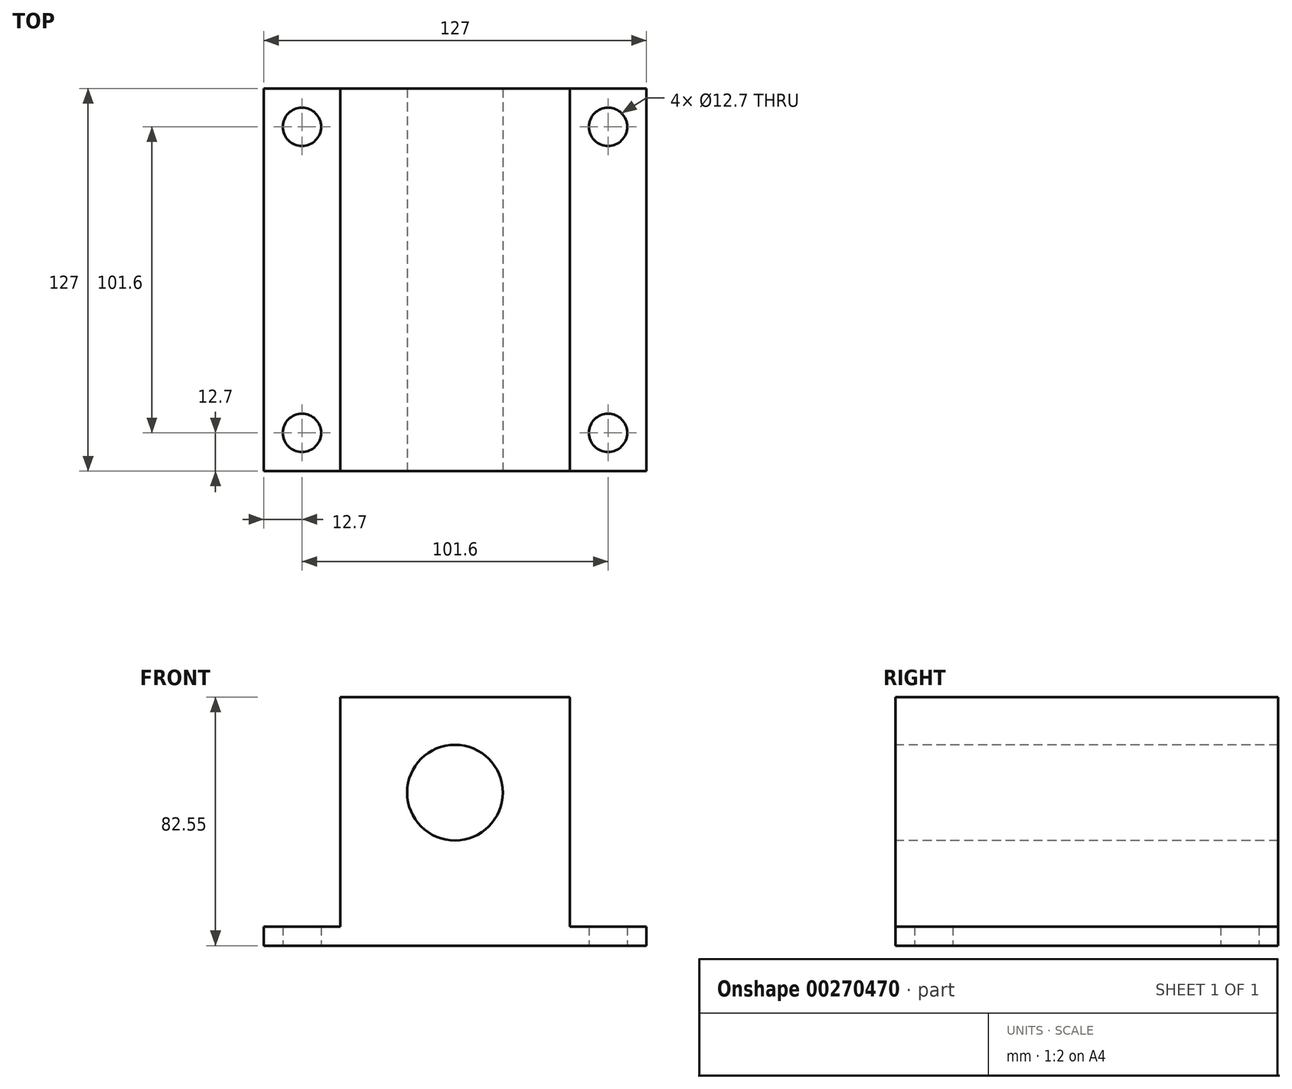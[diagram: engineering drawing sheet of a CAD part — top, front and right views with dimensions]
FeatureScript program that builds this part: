
annotation { "Feature Type Name" : "Feature", "Feature Type Description" : "" }
export const myFeature = defineFeature(function(context is Context, id is Id, definition is map)
    precondition{}
    {
        {
            var Q0;
            Q0=qCreatedBy(makeId("Top.planeOp"),FACE);
            var sketch = newSketch(context, id + "F0", { "sketchPlane" : qUnion([Q0])});
            skLineSegment(sketch, "E0.bottom", {"start": v(63.5, -63.5) * mm, "end": v(-63.5, -63.5) * mm});
            skLineSegment(sketch, "E0.top", {"start": v(63.5, 63.5) * mm, "end": v(-63.5, 63.5) * mm});
            skLineSegment(sketch, "E0.left", {"start": v(63.5, -63.5) * mm, "end": v(63.5, 63.5) * mm});
            skLineSegment(sketch, "E0.right", {"start": v(-63.5, -63.5) * mm, "end": v(-63.5, 63.5) * mm});
            skPoint(sketch, "E0.middle", {"position": v(0, 0) * mm});
            skLineSegment(sketch, "E1.bottom", {"start": v(50.8, 50.8) * mm, "end": v(-50.8, 50.8) * mm, "construction": true});
            skLineSegment(sketch, "E1.top", {"start": v(50.8, -50.8) * mm, "end": v(-50.8, -50.8) * mm, "construction": true});
            skLineSegment(sketch, "E1.left", {"start": v(50.8, 50.8) * mm, "end": v(50.8, -50.8) * mm, "construction": true});
            skLineSegment(sketch, "E1.right", {"start": v(-50.8, 50.8) * mm, "end": v(-50.8, -50.8) * mm, "construction": true});
            skCircle(sketch, "E2", {"center": v(-50.8, -50.8) * mm, "radius": 6.35 * mm});
            skCircle(sketch, "E3", {"center": v(-50.8, 50.8) * mm, "radius": 6.35 * mm});
            skCircle(sketch, "E4", {"center": v(50.8, 50.8) * mm, "radius": 6.35 * mm});
            skCircle(sketch, "E5", {"center": v(50.8, -50.8) * mm, "radius": 6.35 * mm});
            skSolve(sketch);
        }
        {
            var Q0;
            Q0 = qSketchRegion(id + "F0", true);
            extrude(context, id + "F1", {"entities" : qUnion([Q0]), "depth" : 6.35 * mm});
        }
        {
            var Q0;
            Q0=makeQuery(id+"F1.opExtrude","SWEPT_FACE",FACE,{"disambiguationData":[OSD([sQuery(id+"F0.wireOp",EDGE,"E0.bottom")])]});
            var sketch = newSketch(context, id + "F2", { "sketchPlane" : qUnion([Q0])});
            skLineSegment(sketch, "E6.bottom", {"start": v(-38.1, 6.35) * mm, "end": v(38.1, 6.35) * mm});
            skLineSegment(sketch, "E6.top", {"start": v(-38.1, 82.55) * mm, "end": v(38.1, 82.55) * mm});
            skLineSegment(sketch, "E6.left", {"start": v(-38.1, 6.35) * mm, "end": v(-38.1, 82.55) * mm});
            skLineSegment(sketch, "E6.right", {"start": v(38.1, 6.35) * mm, "end": v(38.1, 82.55) * mm});
            skLineSegment(sketch, "E7", {"start": v(0, 82.55) * mm, "end": v(0, 6.35) * mm, "construction": true});
            skCircle(sketch, "E8", {"center": v(0, 50.8) * mm, "radius": 15.88 * mm});
            skSolve(sketch);
        }
        {
            var Q0;
            Q0 = qSketchRegion(id + "F2", true);
            var Q1;
            Q1=makeQuery(id+"F1.opExtrude","SWEPT_FACE",FACE,{"disambiguationData":[OSD([sQuery(id+"F0.wireOp",EDGE,"E0.top")])]});
            extrude(context, id + "F3", {"entities" : qUnion([Q0]), "operationType" : NewBodyOperationType.ADD, "endBound" : BoundingType.UP_TO_SURFACE, "oppositeDirection" : true, "endBoundEntityFace" : qUnion([Q1]), "depth" : 25.4 * mm});
        }
    });
